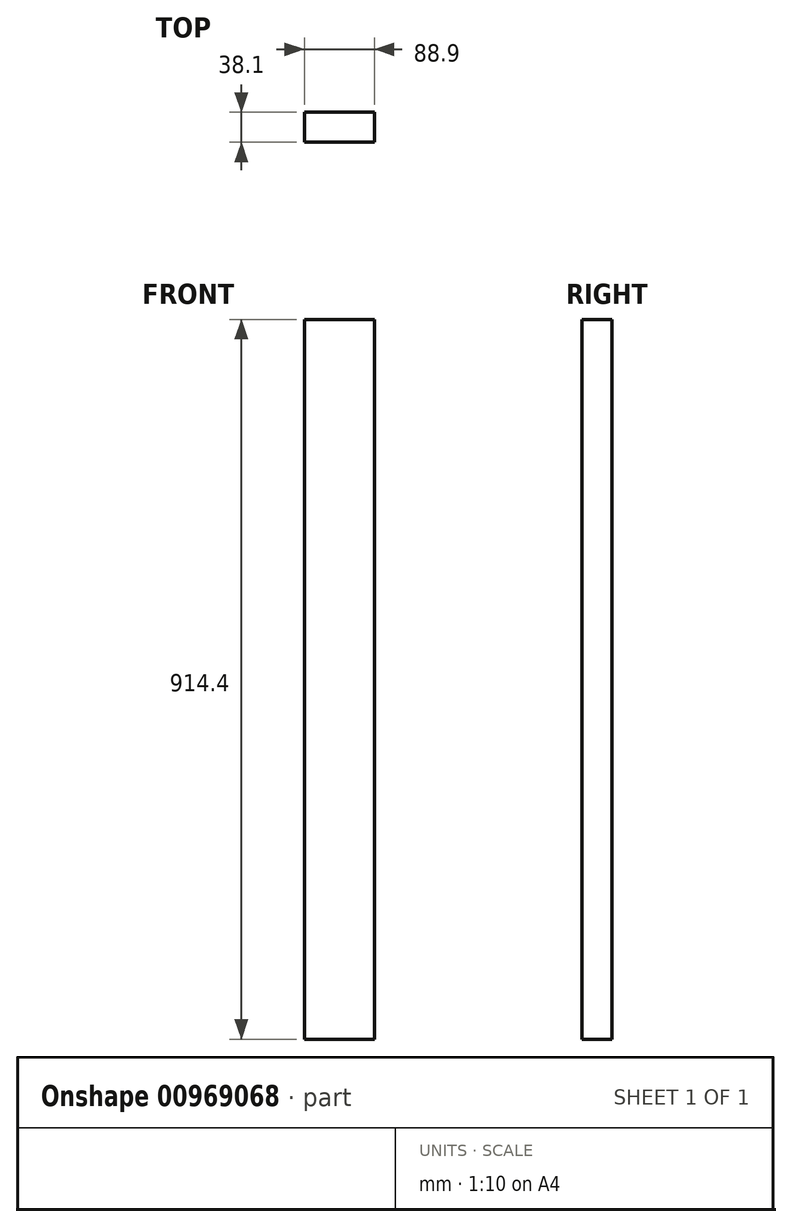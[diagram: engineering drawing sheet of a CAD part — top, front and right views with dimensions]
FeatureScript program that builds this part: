
annotation { "Feature Type Name" : "Feature", "Feature Type Description" : "" }
export const myFeature = defineFeature(function(context is Context, id is Id, definition is map)
    precondition{}
    {
        {
            var Q0;
            Q0=qCreatedBy(makeId("Top.planeOp"),FACE);
            var sketch = newSketch(context, id + "F0", { "sketchPlane" : qUnion([Q0])});
            skLineSegment(sketch, "E0.bottom", {"start": v(0, 0) * mm, "end": v(88.9, 0) * mm});
            skLineSegment(sketch, "E0.top", {"start": v(0, -38.1) * mm, "end": v(88.9, -38.1) * mm});
            skLineSegment(sketch, "E0.left", {"start": v(0, 0) * mm, "end": v(0, -38.1) * mm});
            skLineSegment(sketch, "E0.right", {"start": v(88.9, 0) * mm, "end": v(88.9, -38.1) * mm});
            skSolve(sketch);
        }
        {
            var Q0;
            Q0=makeQuery(id+"F0.imprint","IMPRINT",FACE,{"disambiguationData":[TD([[makeQuery(id+"F0.imprint","IMPRINT",EDGE,{"derivedFrom":sQuery(id+"F0.wireOp",EDGE,"E0.bottom")}),-1.0]])]});
            extrude(context, id + "F1", {"entities" : qUnion([Q0]), "depth" : 914.4 * mm, "offsetDistance" : 25.4 * mm});
        }
    });
